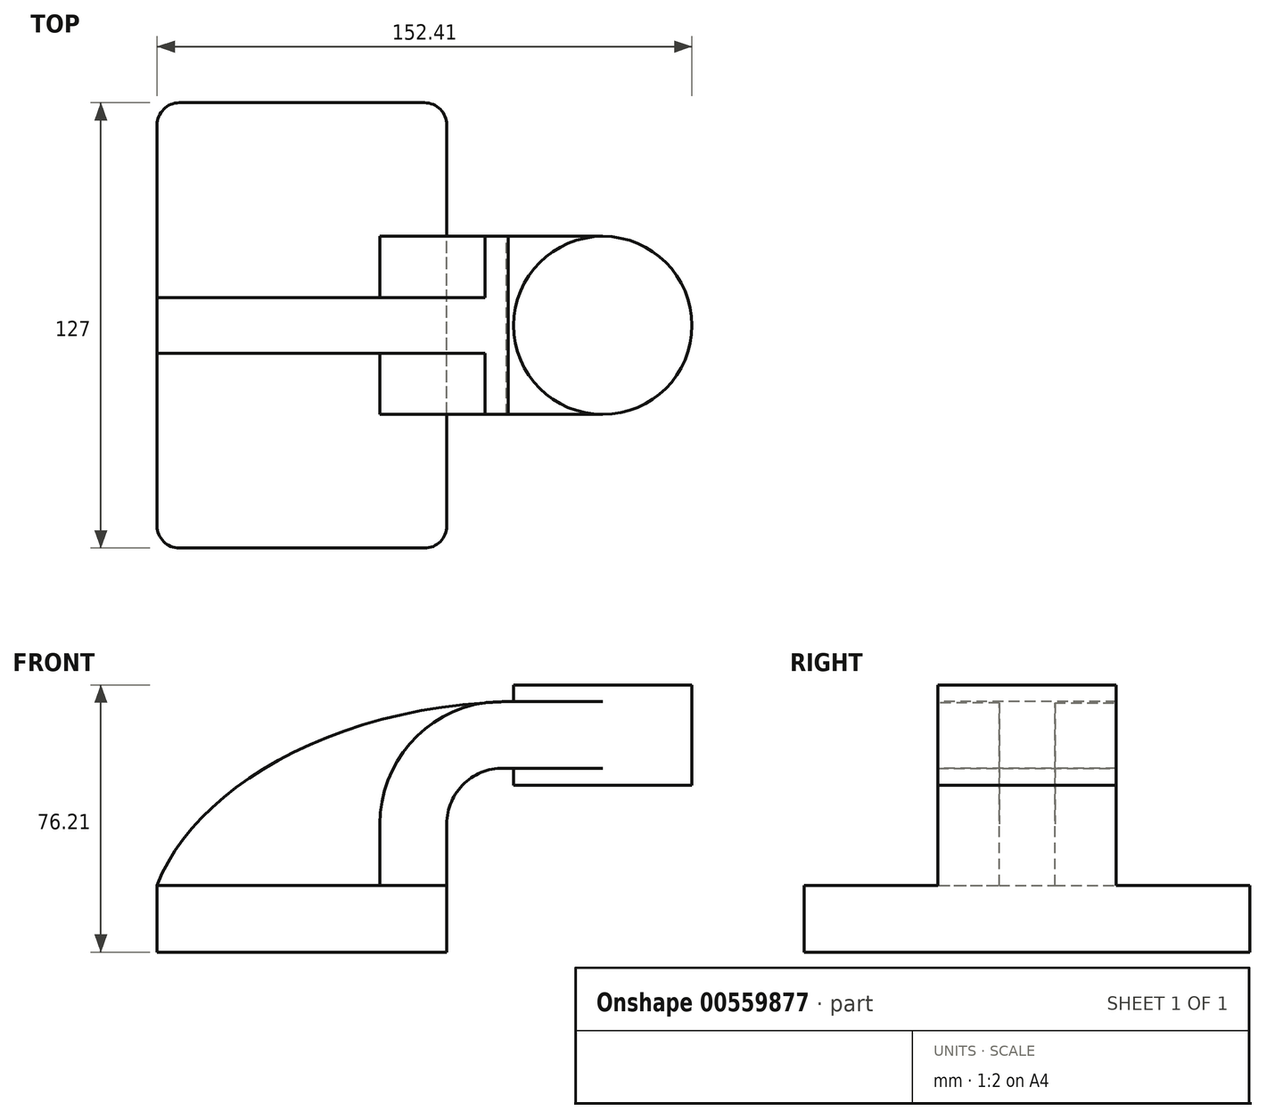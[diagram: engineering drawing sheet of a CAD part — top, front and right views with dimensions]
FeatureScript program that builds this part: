
annotation { "Feature Type Name" : "Feature", "Feature Type Description" : "" }
export const myFeature = defineFeature(function(context is Context, id is Id, definition is map)
    precondition{}
    {
        {
            var Q0;
            Q0=qCreatedBy(makeId("Front.planeOp"),FACE);
            var sketch = newSketch(context, id + "F0", { "sketchPlane" : qUnion([Q0])});
            skLineSegment(sketch, "E0.bottom", {"start": v(-41.28, -9.53) * mm, "end": v(41.28, -9.53) * mm});
            skLineSegment(sketch, "E0.top", {"start": v(-41.28, 9.52) * mm, "end": v(41.27, 9.52) * mm});
            skLineSegment(sketch, "E0.left", {"start": v(-41.27, -9.53) * mm, "end": v(-41.28, 9.52) * mm});
            skLineSegment(sketch, "E0.right", {"start": v(41.28, -9.53) * mm, "end": v(41.27, 9.53) * mm});
            skPoint(sketch, "E0.middle", {"position": v(0, 0) * mm});
            skLineSegment(sketch, "E1.bottom", {"start": v(60.32, 38.1) * mm, "end": v(111.12, 38.1) * mm});
            skLineSegment(sketch, "E1.top", {"start": v(60.32, 66.67) * mm, "end": v(111.12, 66.67) * mm});
            skLineSegment(sketch, "E1.left", {"start": v(60.32, 38.1) * mm, "end": v(60.32, 66.67) * mm});
            skLineSegment(sketch, "E1.right", {"start": v(111.12, 38.1) * mm, "end": v(111.12, 66.67) * mm});
            skPoint(sketch, "E1.middle", {"position": v(85.72, 52.39) * mm});
            skLineSegment(sketch, "E2", {"start": v(41.27, 9.53) * mm, "end": v(41.27, 27.04) * mm});
            skArc(sketch, "E3", {"start": v(41.27, 27.04) * mm, "mid": v(46.3, 38.63) * mm, "end": v(58.2, 42.88) * mm});
            skLineSegment(sketch, "E4", {"start": v(58.2, 42.88) * mm, "end": v(85.72, 42.88) * mm});
            skLineSegment(sketch, "E5.0", {"start": v(58.72, 61.93) * mm, "end": v(85.72, 61.93) * mm});
            skArc(sketch, "E5.1", {"start": v(22.22, 27.04) * mm, "mid": v(33.02, 52.28) * mm, "end": v(58.72, 61.93) * mm});
            skLineSegment(sketch, "E5.2", {"start": v(22.22, 9.53) * mm, "end": v(22.22, 27.04) * mm});
            skLineSegment(sketch, "E6", {"start": v(85.72, 42.88) * mm, "end": v(85.72, 52.39) * mm});
            skLineSegment(sketch, "E7", {"start": v(85.72, 52.39) * mm, "end": v(85.72, 61.93) * mm});
            skFitSpline(sketch, "E8", {"points": [v(-41.28, 9.53) * mm, v(58.72, 61.93) * mm], "startDerivative": vector(30.38, 80.24) * mm, "endDerivative": vector(153.94, 4.68) * mm});
            skLineSegment(sketch, "E9", {"start": v(85.72, 66.67) * mm, "end": v(85.72, 38.1) * mm});
            skSolve(sketch);
        }
        {
            var Q0;
            Q0=makeQuery(id+"F0.imprint","IMPRINT",FACE,{"disambiguationData":[TD([[makeQuery(id+"F0.imprint","IMPRINT",EDGE,{"derivedFrom":sQuery(id+"F0.wireOp",EDGE,"E0.bottom")}),1.0]])]});
            extrude(context, id + "F1", {"entities" : qUnion([Q0]), "endBound" : BoundingType.SYMMETRIC, "depth" : 127 * mm, "offsetDistance" : 25.4 * mm});
        }
        {
            var Q0;
            {var subQ1=sQuery(id+"F0.wireOp",EDGE,"E2");Q0=makeQuery(id+"F0.imprint","IMPRINT",FACE,{"disambiguationData":[TD([[makeQuery(id+"F0.imprint","IMPRINT",EDGE,{"derivedFrom":subQ1}),1.0]])]});}
            var Q1;
            {var subQ0=sQuery(id+"F0.wireOp",EDGE,"E4");var subQ1=sQuery(id+"F0.wireOp",EDGE,"E1.left");var subQ2=makeQuery(id+"F0.imprint","INTERSECT",VERTEX,{"derivedFrom":[subQ1,subQ0]});Q1=makeQuery(id+"F0.imprint","IMPRINT",FACE,{"disambiguationData":[TD([[makeQuery(id+"F0.imprint","IMPRINT",EDGE,{"disambiguationData":[TD([[subQ2,-1.0]])],"derivedFrom":subQ1}),-1.0]])]});}
            extrude(context, id + "F2", {"entities" : qUnion([Q0, Q1]), "operationType" : NewBodyOperationType.ADD, "endBound" : BoundingType.SYMMETRIC, "depth" : 50.8 * mm, "offsetDistance" : 25.4 * mm});
        }
        {
            var Q0;
            {var subQ3=sQuery(id+"F0.wireOp",EDGE,"E5.2");Q0=makeQuery(id+"F0.imprint","IMPRINT",FACE,{"disambiguationData":[TD([[makeQuery(id+"F0.imprint","IMPRINT",EDGE,{"derivedFrom":subQ3}),1.0]])]});}
            extrude(context, id + "F3", {"entities" : qUnion([Q0]), "operationType" : NewBodyOperationType.ADD, "endBound" : BoundingType.SYMMETRIC, "depth" : 15.88 * mm, "offsetDistance" : 25.4 * mm});
        }
        {
            var Q0;
            {var subQ4=sQuery(id+"F0.wireOp",EDGE,"E1.right");Q0=makeQuery(id+"F0.imprint","IMPRINT",FACE,{"disambiguationData":[TD([[makeQuery(id+"F0.imprint","IMPRINT",EDGE,{"derivedFrom":subQ4}),1.0]])]});}
            var Q1;
            Q1=sQuery(id+"F0.wireOp",EDGE,"E9");
            revolve(context, id + "F4", {"operationType" : NewBodyOperationType.ADD, "entities" : qUnion([Q0]), "axis" : qUnion([Q1]), "revolveType" : RevolveType.FULL});
        }
        {
            var Q0;
            Q0=makeQuery(id+"F1.opExtrude","CAP_EDGE",EDGE,{"disambiguationData":[OSD([sQuery(id+"F0.wireOp",EDGE,"E0.left")])],"isStart":false});
            var Q1;
            Q1=makeQuery(id+"F1.opExtrude","CAP_EDGE",EDGE,{"disambiguationData":[OSD([sQuery(id+"F0.wireOp",EDGE,"E0.right")])],"isStart":false});
            var Q2;
            Q2=makeQuery(id+"F1.opExtrude","CAP_EDGE",EDGE,{"disambiguationData":[OSD([sQuery(id+"F0.wireOp",EDGE,"E0.right")])],"isStart":true});
            var Q3;
            Q3=makeQuery(id+"F1.opExtrude","CAP_EDGE",EDGE,{"disambiguationData":[OSD([sQuery(id+"F0.wireOp",EDGE,"E0.left")])],"isStart":true});
            fillet(context, id + "F5", {"entities" : qUnion([Q0, Q1, Q2, Q3]), "radius" : 6.35 * mm, "tangentPropagation" : true, "allowEdgeOverflow" : false});
        }
    });
